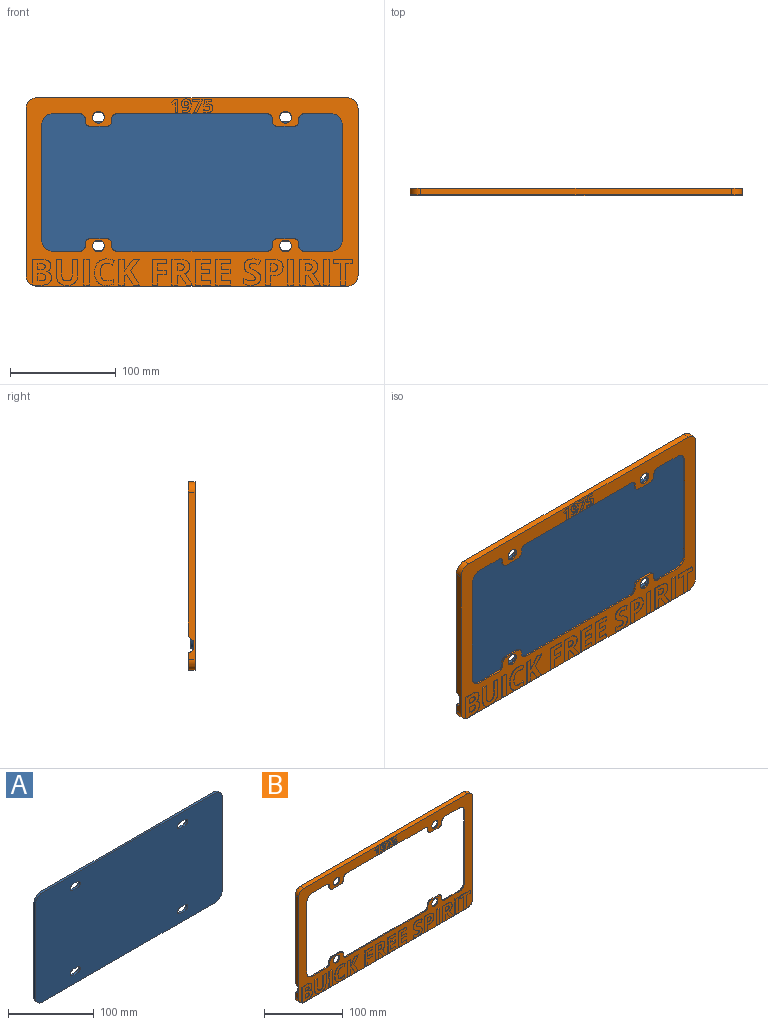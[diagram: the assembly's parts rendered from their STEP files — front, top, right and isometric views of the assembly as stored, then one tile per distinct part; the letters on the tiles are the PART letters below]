
ASSEMBLY  parts=2 mates=1
PART A: 26 faces, bbox 308x3x156 mm
  f0: plane 284x3mm, normal (0,0,1), area 852mm2, adj f1,f23,f24,f25
  f1: cylinder r=12mm len=12mm, axis (0,1,0), area 56.5mm2, adj f0,f2,f24,f25
  f2: plane 132x3mm, normal (-1,0,0), area 396mm2, adj f1,f3,f24,f25
  f3: cylinder r=12mm len=12mm, axis (0,1,0), area 56.5mm2, adj f2,f4,f24,f25
  f4: plane 284x3mm, normal (0,0,-1), area 852mm2, adj f3,f5,f24,f25
  f5: cylinder r=12mm len=12mm, axis (0,1,0), area 56.5mm2, adj f4,f6,f24,f25
  f6: plane 132x3mm, normal (1,0,0), area 396mm2, adj f5,f23,f24,f25
  f7: plane 8x3mm, normal (0,0,-1), area 24mm2, adj f8,f19,f24,f25
  f8: cylinder r=4.25mm len=8.5mm, axis (0,1,0), area 40.1mm2, adj f7,f9,f24,f25
  f9: plane 8x3mm, normal (0,0,1), area 24mm2, adj f8,f19,f24,f25
  f10: cylinder r=4.25mm len=8.5mm, axis (0,1,0), area 40.1mm2, adj f11,f20,f24,f25
  f11: plane 8x3mm, normal (0,0,1), area 24mm2, adj f10,f12,f24,f25
  f12: cylinder r=4.25mm len=8.5mm, axis (0,1,0), area 40.1mm2, adj f11,f20,f24,f25
  f13: plane 8x3mm, normal (0,0,-1), area 24mm2, adj f14,f21,f24,f25
  f14: cylinder r=4.25mm len=8.5mm, axis (0,1,0), area 40.1mm2, adj f13,f15,f24,f25
  f15: plane 8x3mm, normal (0,0,1), area 24mm2, adj f14,f21,f24,f25
  f16: cylinder r=4.25mm len=8.5mm, axis (0,1,0), area 40.1mm2, adj f17,f22,f24,f25
  f17: plane 8x3mm, normal (0,0,-1), area 24mm2, adj f16,f18,f24,f25
  f18: cylinder r=4.25mm len=8.5mm, axis (0,1,0), area 40.1mm2, adj f17,f22,f24,f25
  f19: cylinder r=4.25mm len=8.5mm, axis (0,1,0), area 40.1mm2, adj f7,f9,f24,f25
  f20: plane 8x3mm, normal (0,0,-1), area 24mm2, adj f10,f12,f24,f25
  f21: cylinder r=4.25mm len=8.5mm, axis (0,1,0), area 40.1mm2, adj f13,f15,f24,f25
  f22: plane 8x3mm, normal (0,0,1), area 24mm2, adj f16,f18,f24,f25
  f23: cylinder r=12mm len=12mm, axis (0,1,0), area 56.5mm2, adj f0,f6,f24,f25
  f24: plane 308x156mm, normal (0,-1,0), area 47425.4mm2, adj f0,f1,f2,f3,f4,f5,f6,f7
  f25: plane 308x156mm, normal (0,1,0), area 47425.4mm2, adj f0,f1,f2,f3,f4,f5,f6,f7
PART B: 372 faces, bbox 314x7x178 mm
  f0: plane 314x178mm, normal (0,-1,0), area 16011.1mm2, adj f2,f3,f4,f5,f6,f7,f8,f9
  f1: plane 314x152mm, normal (0,1,0), area 10253mm2, adj f2,f3,f4,f5,f8,f9,f10,f11
  f2: plane 26x1.6mm, normal (0,0,1), area 41.6mm2, adj f0,f1,f16,f32
  f3: plane 142x1.6mm, normal (0,0,1), area 227.2mm2, adj f0,f1,f31,f35
  f4: plane 142x1.6mm, normal (0,0,-1), area 227.2mm2, adj f0,f1,f39,f45
  f5: plane 26x1.6mm, normal (0,0,-1), area 41.6mm2, adj f0,f1,f12,f43
  f6: plane 294x6.4mm, normal (0,0,1), area 1881.6mm2, adj f0,f7,f18,f126
  f7: cylinder r=10mm len=10mm, axis (0,1,0), area 100.5mm2, adj f0,f6,f8,f126
  f8: plane 158x6.4mm, normal (-1,0,0), area 953mm2, adj f0,f1,f7,f120,f126,f128,f137,f369
  f9: plane 158x6.4mm, normal (1,0,0), area 953mm2, adj f0,f1,f18,f121,f126,f127,f139,f369
  f10: cylinder r=10mm len=10mm, axis (0,1,0), area 25.1mm2, adj f0,f1,f11,f17
  f11: plane 110x1.6mm, normal (1,0,0), area 176mm2, adj f0,f1,f10,f12
  f12: cylinder r=10mm len=10mm, axis (0,1,0), area 25.1mm2, adj f0,f1,f5,f11
  f13: plane 26x1.6mm, normal (0,0,-1), area 41.6mm2, adj f0,f1,f14,f41
  f14: cylinder r=10mm len=10mm, axis (0,1,0), area 25.1mm2, adj f0,f1,f13,f15
  f15: plane 110x1.6mm, normal (-1,0,0), area 176mm2, adj f0,f1,f14,f16
  f16: cylinder r=10mm len=10mm, axis (0,1,0), area 25.1mm2, adj f0,f1,f2,f15
  f17: plane 26x1.6mm, normal (0,0,1), area 41.6mm2, adj f0,f1,f10,f37
  f18: cylinder r=10mm len=10mm, axis (0,1,0), area 100.5mm2, adj f0,f6,f9,f126
  f19: plane 2x1.6mm, normal (-1,0,0), area 3.2mm2, adj f0,f1,f43,f44
  f20: plane 15x1.6mm, normal (0,0,-1), area 24mm2, adj f0,f1,f44,f46
  f21: plane 2x1.6mm, normal (1,0,0), area 3.2mm2, adj f0,f1,f45,f46
  f22: plane 2x1.6mm, normal (-1,0,0), area 3.2mm2, adj f0,f1,f39,f40
  f23: plane 15x1.6mm, normal (0,0,-1), area 24mm2, adj f0,f1,f40,f42
  f24: plane 2x1.6mm, normal (1,0,0), area 3.2mm2, adj f0,f1,f41,f42
  f25: plane 2x1.6mm, normal (1,0,0), area 3.2mm2, adj f0,f1,f35,f36
  f26: plane 15x1.6mm, normal (0,0,1), area 24mm2, adj f0,f1,f36,f38
  f27: plane 2x1.6mm, normal (-1,0,0), area 3.2mm2, adj f0,f1,f37,f38
  f28: plane 2x1.6mm, normal (-1,0,0), area 3.2mm2, adj f0,f1,f31,f33
  f29: plane 2x1.6mm, normal (1,0,0), area 3.2mm2, adj f0,f1,f32,f34
  f30: plane 15x1.6mm, normal (0,0,1), area 24mm2, adj f0,f1,f33,f34
  f31: cylinder r=5mm len=5mm, axis (0,-1,0), area 12.6mm2, adj f0,f1,f3,f28
  f32: cylinder r=5mm len=5mm, axis (0,1,0), area 12.6mm2, adj f0,f1,f2,f29
  f33: cylinder r=5mm len=5mm, axis (0,-1,0), area 12.6mm2, adj f0,f1,f28,f30
  f34: cylinder r=5mm len=5mm, axis (0,1,0), area 12.6mm2, adj f0,f1,f29,f30
  f35: cylinder r=5mm len=5mm, axis (0,1,0), area 12.6mm2, adj f0,f1,f3,f25
  f36: cylinder r=5mm len=5mm, axis (0,1,0), area 12.6mm2, adj f0,f1,f25,f26
  f37: cylinder r=5mm len=5mm, axis (0,-1,0), area 12.6mm2, adj f0,f1,f17,f27
  f38: cylinder r=5mm len=5mm, axis (0,-1,0), area 12.6mm2, adj f0,f1,f26,f27
  f39: cylinder r=5mm len=5mm, axis (0,1,0), area 12.6mm2, adj f0,f1,f4,f22
  f40: cylinder r=5mm len=5mm, axis (0,-1,0), area 12.6mm2, adj f0,f1,f22,f23
  f41: cylinder r=5mm len=5mm, axis (0,-1,0), area 12.6mm2, adj f0,f1,f13,f24
  f42: cylinder r=5mm len=5mm, axis (0,1,0), area 12.6mm2, adj f0,f1,f23,f24
  f43: cylinder r=5mm len=5mm, axis (0,1,0), area 12.6mm2, adj f0,f1,f5,f19
  f44: cylinder r=5mm len=5mm, axis (0,-1,0), area 12.6mm2, adj f0,f1,f19,f20
  f45: cylinder r=5mm len=5mm, axis (0,-1,0), area 12.6mm2, adj f0,f1,f4,f21
  f46: cylinder r=5mm len=5mm, axis (0,1,0), area 12.6mm2, adj f0,f1,f20,f21
  f47: cylinder r=5.5mm len=11mm, axis (0,-1,0), area 55.3mm2, adj f0,f1
  f48: cylinder r=5.5mm len=11mm, axis (0,-1,0), area 55.3mm2, adj f0,f1
  f49: cylinder r=5.5mm len=11mm, axis (0,-1,0), area 55.3mm2, adj f0,f1
  f50: cylinder r=5.5mm len=11mm, axis (0,-1,0), area 55.3mm2, adj f0,f1
  f51: plane 2.73x0.6mm, normal (0,0,-1), area 1.6mm2, adj f0,f52,f60,f61
  f52: plane 12.89x0.6mm, normal (1,0,0), area 7.7mm2, adj f0,f51,f53,f61
  f53: plane 2.24x0.6mm, normal (0,0,1), area 1.3mm2, adj f0,f52,f54,f61
  f54: plane 4.15x3.31mm, normal (-0.62,0,0.78), area 3.2mm2, adj f0,f53,f55,f61
  f55: plane 1.64x1.31mm, normal (-0.78,0,-0.63), area 1.3mm2, adj f0,f54,f56,f61
  f56: plane 1.48x1.19mm, normal (0.63,0,-0.78), area 1.1mm2, adj f0,f55,f57,f61
  f57: extruded ~0.94x0.89mm, area 0.8mm2, adj f0,f56,f58,f61
  f58: plane 1.34x0.6mm, normal (-1,0,0.03), area 0.8mm2, adj f0,f57,f59,f61
  f59: plane 1.22x0.6mm, normal (-1,0,0.02), area 0.7mm2, adj f0,f58,f60,f61
  f60: plane 7.46x0.6mm, normal (-1,0,0), area 4.5mm2, adj f0,f51,f59,f61
  f61: plane 12.89x6.39mm, normal (0,-1,0), area 43mm2, adj f51,f52,f53,f54,f55,f56,f57,f58
  f62: extruded ~1.32x0.6mm, area 0.9mm2, adj f63,f87,f88,f89
  f63: extruded ~1.41x0.72mm, area 1mm2, adj f62,f64,f88,f89
  f64: extruded ~1.77x0.6mm, area 1.1mm2, adj f63,f65,f88,f89
  f65: extruded ~1.25x0.6mm, area 0.9mm2, adj f64,f66,f88,f89
  f66: extruded ~1.42x0.6mm, area 0.9mm2, adj f65,f67,f88,f89
  f67: extruded ~1.31x0.6mm, area 0.9mm2, adj f66,f68,f88,f89
  f68: extruded ~1.48x0.6mm, area 0.9mm2, adj f67,f87,f88,f89
  f69: extruded ~5.69x1.6mm, area 3.6mm2, adj f0,f70,f86,f88
  f70: extruded ~3.04x0.6mm, area 1.9mm2, adj f0,f69,f71,f88
  f71: extruded ~1.94x1.64mm, area 1.6mm2, adj f0,f70,f72,f88
  f72: extruded ~2.5x0.67mm, area 1.6mm2, adj f0,f71,f73,f88
  f73: extruded ~3.2x1.2mm, area 2.1mm2, adj f0,f72,f74,f88
  f74: extruded ~3.28x1.18mm, area 2.1mm2, adj f0,f73,f75,f88
  f75: extruded ~3x0.97mm, area 1.9mm2, adj f0,f74,f76,f88
  f76: extruded ~2.65x1.08mm, area 1.8mm2, adj f0,f75,f77,f88
  f77: extruded ~1.67x0.6mm, area 1mm2, adj f0,f76,f78,f88
  f78: extruded ~1.18x1.16mm, area 1mm2, adj f0,f77,f79,f88
  f79: plane 0.6x0.11mm, normal (0,0,-1), area 0.1mm2, adj f0,f78,f80,f88
  f80: extruded ~2.37x0.6mm, area 1.5mm2, adj f0,f79,f81,f88
  f81: extruded ~1.35x1.26mm, area 1.1mm2, adj f0,f80,f82,f88
  f82: extruded ~2.25x0.6mm, area 1.4mm2, adj f0,f81,f83,f88
  f83: extruded ~1.55x0.6mm, area 0.9mm2, adj f0,f82,f84,f88
  f84: plane 2.19x0.6mm, normal (-1,0,0), area 1.3mm2, adj f0,f83,f85,f88
  f85: extruded ~1.74x0.6mm, area 1mm2, adj f0,f84,f86,f88
  f86: extruded ~4.86x1.88mm, area 3.2mm2, adj f0,f69,f85,f88
  f87: extruded ~1.67x0.6mm, area 1.1mm2, adj f62,f68,f88,f89
  f88: plane 13.22x9.1mm, normal (0,-1,0), area 70.9mm2, adj f62,f63,f64,f65,f66,f67,f68,f69
  f89: plane 4.29x3.76mm, normal (0,-1,0), area 13mm2, adj f62,f63,f64,f65,f66,f67,f68,f87
  f90: plane 10.58x4.84mm, normal (-0.91,0,0.42), area 7mm2, adj f0,f91,f96,f97
  f91: plane 2.86x0.6mm, normal (0,0,-1), area 1.7mm2, adj f0,f90,f92,f97
  f92: plane 11.16x4.88mm, normal (0.92,0,-0.4), area 7.3mm2, adj f0,f91,f93,f97
  f93: plane 1.71x0.6mm, normal (1,0,0), area 1mm2, adj f0,f92,f94,f97
  f94: plane 9.25x0.6mm, normal (0,0,1), area 5.5mm2, adj f0,f93,f95,f97
  f95: plane 2.29x0.6mm, normal (-1,0,0), area 1.4mm2, adj f0,f94,f96,f97
  f96: plane 6.36x0.6mm, normal (0,0,-1), area 3.8mm2, adj f0,f90,f95,f97
  f97: plane 12.87x9.25mm, normal (0,-1,0), area 50.2mm2, adj f90,f91,f92,f93,f94,f95,f96
  f98: extruded ~2.98x1.05mm, area 1.9mm2, adj f0,f99,f117,f118
  f99: extruded ~1.33x0.6mm, area 0.8mm2, adj f0,f98,f100,f118
  f100: plane 0.6x0.31mm, normal (-0.2,0,0.98), area 0.2mm2, adj f0,f99,f101,f118
  f101: plane 2.53x0.6mm, normal (1,0,-0.09), area 1.5mm2, adj f0,f100,f102,f118
  f102: plane 4.6x0.6mm, normal (0,0,-1), area 2.8mm2, adj f0,f101,f103,f118
  f103: plane 2.31x0.6mm, normal (1,0,0), area 1.4mm2, adj f0,f102,f104,f118
  f104: plane 6.99x0.6mm, normal (0,0,1), area 4.2mm2, adj f0,f103,f105,f118
  f105: plane 6.57x0.6mm, normal (-1,0,0.07), area 4mm2, adj f0,f104,f106,f118
  f106: plane 1.09x0.6mm, normal (-0.47,0,-0.88), area 0.7mm2, adj f0,f105,f107,f118
  f107: extruded ~0.92x0.6mm, area 0.6mm2, adj f0,f106,f108,f118
  f108: extruded ~1.03x0.6mm, area 0.6mm2, adj f0,f107,f109,f118
  f109: extruded ~2.58x1.95mm, area 2.2mm2, adj f0,f108,f110,f118
  f110: extruded ~2.5x2.05mm, area 2.2mm2, adj f0,f109,f111,f118
  f111: extruded ~1.75x0.6mm, area 1.1mm2, adj f0,f110,f112,f118
  f112: extruded ~1.62x0.6mm, area 1mm2, adj f0,f111,f113,f118
  f113: plane 2.36x0.6mm, normal (-1,0,0), area 1.4mm2, adj f0,f112,f114,f118
  f114: extruded ~3.47x0.7mm, area 2.1mm2, adj f0,f113,f115,f118
  f115: extruded ~3.81x1.17mm, area 2.4mm2, adj f0,f114,f116,f118
  f116: extruded ~3.32x1.33mm, area 2.2mm2, adj f0,f115,f117,f118
  f117: extruded ~2.87x1.11mm, area 1.9mm2, adj f0,f98,f116,f118
  f118: plane 13.07x8.61mm, normal (0,-1,0), area 65.6mm2, adj f98,f99,f100,f101,f102,f103,f104,f105
  f119: plane 137.6x1.8mm, normal (1,0,0), area 171.1mm2, adj f125,f126,f128,f133,f135,f136,f368
  f120: plane 5x0.6mm, normal (0,0,-1), area 2.3mm2, adj f1,f8,f128,f368
  f121: plane 5x0.6mm, normal (0,0,-1), area 2.3mm2, adj f1,f9,f127,f364
  f122: plane 137.6x1.8mm, normal (-1,0,0), area 171.1mm2, adj f123,f126,f127,f129,f131,f132,f364
  f123: cylinder r=8mm len=8mm, axis (0,-1,0), area 22.6mm2, adj f122,f124,f126,f365
  f124: plane 294x1.8mm, normal (0,0,-1), area 529.2mm2, adj f123,f125,f126,f366
  f125: cylinder r=8mm len=8mm, axis (0,-1,0), area 22.6mm2, adj f119,f124,f126,f367
  f126: plane 314x145.8mm, normal (0,1,0), area 1787.7mm2, adj f6,f7,f8,f9,f18,f119,f122,f123
  f127: plane 4.2x4.2mm, normal (0,0.71,-0.71), area 13.1mm2, adj f9,f121,f122,f126,f364
  f128: plane 4.2x4.2mm, normal (0,0.71,-0.71), area 13.1mm2, adj f8,f119,f120,f126,f368
  f129: plane 75x4mm, normal (0,-1,0), area 300mm2, adj f122,f130,f131,f132
  f130: plane 75x1mm, normal (-1,0,0), area 75mm2, adj f126,f129,f131,f132
  f131: plane 4x1mm, normal (0,0,1), area 4mm2, adj f122,f126,f129,f130
  f132: plane 4x1mm, normal (0,0,-1), area 4mm2, adj f122,f126,f129,f130
  f133: plane 75x4mm, normal (0,-1,0), area 300mm2, adj f119,f134,f135,f136
  f134: plane 75x1mm, normal (1,0,0), area 75mm2, adj f126,f133,f135,f136
  f135: plane 4x1mm, normal (0,0,1), area 4mm2, adj f119,f126,f133,f134
  f136: plane 4x1mm, normal (0,0,-1), area 4mm2, adj f119,f126,f133,f134
  f137: cylinder r=10mm len=10mm, axis (0,-1,0), area 100.5mm2, adj f0,f8,f138,f369
  f138: plane 294x6.4mm, normal (0,0,-1), area 1881.6mm2, adj f0,f137,f139,f369
  f139: cylinder r=10mm len=10mm, axis (0,-1,0), area 100.5mm2, adj f0,f9,f138,f369
  f140: plane 6.34x0.6mm, normal (1,0,0), area 3.8mm2, adj f141,f164,f165,f166
  f141: plane 3.2x0.6mm, normal (0,0,-1), area 1.9mm2, adj f140,f142,f165,f166
  f142: extruded ~4.33x3.03mm, area 3.6mm2, adj f141,f143,f165,f166
  f143: extruded ~2.5x1.02mm, area 1.7mm2, adj f142,f144,f165,f166
  f144: extruded ~3.15x0.82mm, area 2mm2, adj f143,f164,f165,f166
  f145: plane 2.99x0.6mm, normal (0,0,1), area 1.8mm2, adj f146,f162,f165,f167
  f146: plane 5.41x0.6mm, normal (1,0,0), area 3.2mm2, adj f145,f147,f165,f167
  f147: plane 2.71x0.6mm, normal (0,0,-1), area 1.6mm2, adj f146,f148,f165,f167
  f148: extruded ~3.24x0.61mm, area 2mm2, adj f147,f149,f165,f167
  f149: extruded ~2.01x1.02mm, area 1.4mm2, adj f148,f150,f165,f167
  f150: extruded ~2.15x0.94mm, area 1.5mm2, adj f149,f162,f165,f167
  f151: plane 7.58x0.6mm, normal (0,0,1), area 4.5mm2, adj f0,f152,f163,f165
  f152: plane 24.34x0.6mm, normal (-1,0,0), area 14.6mm2, adj f0,f151,f153,f165
  f153: plane 9.1x0.6mm, normal (0,0,-1), area 5.5mm2, adj f0,f152,f154,f165
  f154: extruded ~6.54x1.86mm, area 4.2mm2, adj f0,f153,f155,f165
  f155: extruded ~5.19x2.41mm, area 3.6mm2, adj f0,f154,f156,f165
  f156: extruded ~3.76x1.03mm, area 2.4mm2, adj f0,f155,f157,f165
  f157: extruded ~3.34x1.93mm, area 2.4mm2, adj f0,f156,f158,f165
  f158: plane 0.6x0.17mm, normal (1,0,0), area 0.1mm2, adj f0,f157,f159,f165
  f159: extruded ~2.72x1.68mm, area 2mm2, adj f0,f158,f160,f165
  f160: extruded ~3.58x1.02mm, area 2.3mm2, adj f0,f159,f161,f165
  f161: extruded ~4.69x2.34mm, area 3.3mm2, adj f0,f160,f163,f165
  f162: extruded ~3.04x0.65mm, area 1.9mm2, adj f145,f150,f165,f167
  f163: extruded ~7.52x1.47mm, area 4.7mm2, adj f0,f151,f161,f165
  f164: plane 3.36x0.6mm, normal (0,0,1), area 2mm2, adj f140,f144,f165,f166
  f165: plane 24.34x18.05mm, normal (0,-1,0), area 323mm2, adj f140,f141,f142,f143,f144,f145,f146,f147
  f166: plane 7.52x6.34mm, normal (0,-1,0), area 43.3mm2, adj f140,f141,f142,f143,f144,f164
  f167: plane 6.97x5.41mm, normal (0,-1,0), area 34.4mm2, adj f145,f146,f147,f148,f149,f150,f162
  f168: plane 15.75x0.6mm, normal (1,0,0), area 9.4mm2, adj f0,f169,f182,f183
  f169: plane 5.15x0.6mm, normal (0,0,1), area 3.1mm2, adj f0,f168,f170,f183
  f170: plane 14.87x0.6mm, normal (-1,0,0), area 8.9mm2, adj f0,f169,f171,f183
  f171: extruded ~4.15x1.14mm, area 2.6mm2, adj f0,f170,f172,f183
  f172: extruded ~3.67x1.32mm, area 2.4mm2, adj f0,f171,f173,f183
  f173: extruded ~3.75x1.32mm, area 2.5mm2, adj f0,f172,f174,f183
  f174: extruded ~4.13x1.13mm, area 2.6mm2, adj f0,f173,f175,f183
  f175: plane 14.9x0.6mm, normal (1,0,0), area 8.9mm2, adj f0,f174,f176,f183
  f176: plane 5.14x0.6mm, normal (0,0,1), area 3.1mm2, adj f0,f175,f177,f183
  f177: plane 15.68x0.6mm, normal (-1,0,0), area 9.4mm2, adj f0,f176,f178,f183
  f178: extruded ~6.58x2.6mm, area 4.4mm2, adj f0,f177,f179,f183
  f179: extruded ~7.29x2.41mm, area 4.7mm2, adj f0,f178,f180,f183
  f180: extruded ~5.39x1.08mm, area 3.3mm2, adj f0,f179,f181,f183
  f181: extruded ~3.49x3.11mm, area 2.8mm2, adj f0,f180,f182,f183
  f182: extruded ~4.73x1.21mm, area 3mm2, adj f0,f168,f181,f183
  f183: plane 24.68x19.98mm, normal (0,-1,0), area 271.1mm2, adj f168,f169,f170,f171,f172,f173,f174,f175
  f184: plane 24.34x0.6mm, normal (-1,0,0), area 14.6mm2, adj f0,f185,f187,f188
  f185: plane 5.16x0.6mm, normal (0,0,-1), area 3.1mm2, adj f0,f184,f186,f188
  f186: plane 24.34x0.6mm, normal (1,0,0), area 14.6mm2, adj f0,f185,f187,f188
  f187: plane 5.16x0.6mm, normal (0,0,1), area 3.1mm2, adj f0,f184,f186,f188
  f188: plane 24.34x5.16mm, normal (0,-1,0), area 125.6mm2, adj f184,f185,f186,f187
  f189: extruded ~4.51x2.19mm, area 3.1mm2, adj f0,f190,f203,f204
  f190: extruded ~2.71x0.6mm, area 1.7mm2, adj f0,f189,f191,f204
  f191: extruded ~2.75x1.13mm, area 1.8mm2, adj f0,f190,f192,f204
  f192: plane 4.2x1.66mm, normal (0.93,0,-0.37), area 2.7mm2, adj f0,f191,f193,f204
  f193: extruded ~7.12x1.71mm, area 4.4mm2, adj f0,f192,f194,f204
  f194: extruded ~6.07x1.52mm, area 3.8mm2, adj f0,f193,f195,f204
  f195: extruded ~4.38x3.97mm, area 3.6mm2, adj f0,f194,f196,f204
  f196: extruded ~6.65x1.38mm, area 4.1mm2, adj f0,f195,f197,f204
  f197: extruded ~9.25x2.81mm, area 5.9mm2, adj f0,f196,f198,f204
  f198: extruded ~8.12x3.22mm, area 5.4mm2, adj f0,f197,f199,f204
  f199: extruded ~6.69x1.25mm, area 4.1mm2, adj f0,f198,f200,f204
  f200: plane 4.33x0.6mm, normal (1,0,0), area 2.6mm2, adj f0,f199,f201,f204
  f201: extruded ~6.21x1.28mm, area 3.8mm2, adj f0,f200,f202,f204
  f202: extruded ~8.14x6.11mm, area 7mm2, adj f0,f201,f203,f204
  f203: extruded ~6.1x1.6mm, area 3.8mm2, adj f0,f189,f202,f204
  f204: plane 25.02x18.54mm, normal (0,-1,0), area 208mm2, adj f189,f190,f191,f192,f193,f194,f195,f196
  f205: plane 5.86x0.6mm, normal (0,0,-1), area 3.5mm2, adj f0,f206,f217,f218
  f206: plane 13.57x8.56mm, normal (0.85,0,0.53), area 9.6mm2, adj f0,f205,f207,f218
  f207: plane 10.77x8.49mm, normal (0.79,0,-0.62), area 8.2mm2, adj f0,f206,f208,f218
  f208: plane 5.73x0.6mm, normal (0,0,1), area 3.4mm2, adj f0,f207,f209,f218
  f209: plane 8.27x6.6mm, normal (-0.78,0,0.62), area 6.3mm2, adj f0,f208,f210,f218
  f210: plane 2.87x2.03mm, normal (-0.82,0,0.58), area 2.1mm2, adj f0,f209,f211,f218
  f211: plane 11.14x0.6mm, normal (1,0,0), area 6.7mm2, adj f0,f210,f212,f218
  f212: plane 5.16x0.6mm, normal (0,0,1), area 3.1mm2, adj f0,f211,f213,f218
  f213: plane 24.34x0.6mm, normal (-1,0,0), area 14.6mm2, adj f0,f212,f214,f218
  f214: plane 5.16x0.6mm, normal (0,0,-1), area 3.1mm2, adj f0,f213,f215,f218
  f215: plane 8.69x0.6mm, normal (1,0,0), area 5.2mm2, adj f0,f214,f216,f218
  f216: plane 2.18x1.57mm, normal (0.58,0,-0.81), area 1.6mm2, adj f0,f215,f217,f218
  f217: plane 10.25x6.38mm, normal (-0.85,0,-0.53), area 7.2mm2, adj f0,f205,f216,f218
  f218: plane 24.34x19.58mm, normal (0,-1,0), area 271.7mm2, adj f205,f206,f207,f208,f209,f210,f211,f212
  f219: plane 5.08x0.6mm, normal (0,0,-1), area 3mm2, adj f0,f220,f228,f229
  f220: plane 9.62x0.6mm, normal (1,0,0), area 5.8mm2, adj f0,f219,f221,f229
  f221: plane 8.26x0.6mm, normal (0,0,-1), area 5mm2, adj f0,f220,f222,f229
  f222: plane 4.21x0.6mm, normal (1,0,0), area 2.5mm2, adj f0,f221,f223,f229
  f223: plane 8.26x0.6mm, normal (0,0,1), area 5mm2, adj f0,f222,f224,f229
  f224: plane 6.28x0.6mm, normal (1,0,0), area 3.8mm2, adj f0,f223,f225,f229
  f225: plane 8.88x0.6mm, normal (0,0,-1), area 5.3mm2, adj f0,f224,f226,f229
  f226: plane 4.23x0.6mm, normal (1,0,0), area 2.5mm2, adj f0,f225,f227,f229
  f227: plane 13.95x0.6mm, normal (0,0,1), area 8.4mm2, adj f0,f226,f228,f229
  f228: plane 24.34x0.6mm, normal (-1,0,0), area 14.6mm2, adj f0,f219,f227,f229
  f229: plane 24.34x13.95mm, normal (0,-1,0), area 195.9mm2, adj f219,f220,f221,f222,f223,f224,f225,f226
  f230: plane 9.34x0.6mm, normal (1,0,0), area 5.6mm2, adj f0,f231,f248,f249
  f231: plane 2.74x0.6mm, normal (0,0,-1), area 1.6mm2, adj f0,f230,f232,f249
  f232: plane 9.34x5.81mm, normal (-0.85,0,-0.53), area 6.6mm2, adj f0,f231,f233,f249
  f233: plane 5.73x0.6mm, normal (0,0,-1), area 3.4mm2, adj f0,f232,f234,f249
  f234: extruded ~10.61x7.16mm, area 7.7mm2, adj f0,f233,f235,f249
  f235: extruded ~3.35x2.62mm, area 2.6mm2, adj f0,f234,f236,f249
  f236: extruded ~3.82x1.18mm, area 2.4mm2, adj f0,f235,f237,f249
  f237: extruded ~5.49x2.38mm, area 3.7mm2, adj f0,f236,f238,f249
  f238: extruded ~7.34x1.81mm, area 4.6mm2, adj f0,f237,f239,f249
  f239: plane 7.09x0.6mm, normal (0,0,1), area 4.3mm2, adj f0,f238,f240,f249
  f240: plane 24.34x0.6mm, normal (-1,0,0), area 14.6mm2, adj f0,f239,f248,f249
  f241: plane 1.66x0.6mm, normal (0,0,1), area 1mm2, adj f242,f247,f249,f250
  f242: plane 6.57x0.6mm, normal (1,0,0), area 3.9mm2, adj f241,f243,f249,f250
  f243: plane 1.57x0.6mm, normal (0,0,-1), area 0.9mm2, adj f242,f244,f249,f250
  f244: extruded ~3.68x0.73mm, area 2.3mm2, adj f243,f245,f249,f250
  f245: extruded ~2.46x1.19mm, area 1.7mm2, adj f244,f246,f249,f250
  f246: extruded ~2.56x1.16mm, area 1.8mm2, adj f245,f247,f249,f250
  f247: extruded ~3.61x0.82mm, area 2.3mm2, adj f241,f246,f249,f250
  f248: plane 5.16x0.6mm, normal (0,0,-1), area 3.1mm2, adj f0,f230,f240,f249
  f249: plane 24.34x19.44mm, normal (0,-1,0), area 289.3mm2, adj f230,f231,f232,f233,f234,f235,f236,f237
  f250: plane 6.57x6.44mm, normal (0,-1,0), area 37.4mm2, adj f241,f242,f243,f244,f245,f246,f247
  f251: plane 14.02x0.6mm, normal (0,0,-1), area 8.4mm2, adj f0,f252,f262,f263
  f252: plane 4.26x0.6mm, normal (1,0,0), area 2.6mm2, adj f0,f251,f253,f263
  f253: plane 8.85x0.6mm, normal (0,0,1), area 5.3mm2, adj f0,f252,f254,f263
  f254: plane 6.28x0.6mm, normal (1,0,0), area 3.8mm2, adj f0,f253,f255,f263
  f255: plane 8.24x0.6mm, normal (0,0,-1), area 4.9mm2, adj f0,f254,f256,f263
  f256: plane 4.23x0.6mm, normal (1,0,0), area 2.5mm2, adj f0,f255,f257,f263
  f257: plane 8.24x0.6mm, normal (0,0,1), area 4.9mm2, adj f0,f256,f258,f263
  f258: plane 5.34x0.6mm, normal (1,0,0), area 3.2mm2, adj f0,f257,f259,f263
  f259: plane 8.85x0.6mm, normal (0,0,-1), area 5.3mm2, adj f0,f258,f260,f263
  f260: plane 4.23x0.6mm, normal (1,0,0), area 2.5mm2, adj f0,f259,f261,f263
  f261: plane 14.02x0.6mm, normal (0,0,1), area 8.4mm2, adj f0,f260,f262,f263
  f262: plane 24.34x0.6mm, normal (-1,0,0), area 14.6mm2, adj f0,f251,f261,f263
  f263: plane 24.34x14.02mm, normal (0,-1,0), area 235.7mm2, adj f251,f252,f253,f254,f255,f256,f257,f258
  f264: plane 14.02x0.6mm, normal (0,0,-1), area 8.4mm2, adj f0,f265,f275,f276
  f265: plane 4.26x0.6mm, normal (1,0,0), area 2.6mm2, adj f0,f264,f266,f276
  f266: plane 8.85x0.6mm, normal (0,0,1), area 5.3mm2, adj f0,f265,f267,f276
  f267: plane 6.28x0.6mm, normal (1,0,0), area 3.8mm2, adj f0,f266,f268,f276
  f268: plane 8.24x0.6mm, normal (0,0,-1), area 4.9mm2, adj f0,f267,f269,f276
  f269: plane 4.23x0.6mm, normal (1,0,0), area 2.5mm2, adj f0,f268,f270,f276
  f270: plane 8.24x0.6mm, normal (0,0,1), area 4.9mm2, adj f0,f269,f271,f276
  f271: plane 5.34x0.6mm, normal (1,0,0), area 3.2mm2, adj f0,f270,f272,f276
  f272: plane 8.85x0.6mm, normal (0,0,-1), area 5.3mm2, adj f0,f271,f273,f276
  f273: plane 4.23x0.6mm, normal (1,0,0), area 2.5mm2, adj f0,f272,f274,f276
  f274: plane 14.02x0.6mm, normal (0,0,1), area 8.4mm2, adj f0,f273,f275,f276
  f275: plane 24.34x0.6mm, normal (-1,0,0), area 14.6mm2, adj f0,f264,f274,f276
  f276: plane 24.34x14.02mm, normal (0,-1,0), area 235.7mm2, adj f264,f265,f266,f267,f268,f269,f270,f271
  f277: extruded ~5.2x2.37mm, area 3.6mm2, adj f0,f278,f304,f305
  f278: extruded ~4.02x1.27mm, area 2.6mm2, adj f0,f277,f279,f305
  f279: extruded ~4.68x3.27mm, area 3.5mm2, adj f0,f278,f280,f305
  f280: extruded ~3.27x1.7mm, area 2.2mm2, adj f0,f279,f281,f305
  f281: extruded ~1.01x0.98mm, area 0.9mm2, adj f0,f280,f282,f305
  f282: extruded ~1.19x0.6mm, area 0.7mm2, adj f0,f281,f283,f305
  f283: extruded ~1.78x0.78mm, area 1.2mm2, adj f0,f282,f284,f305
  f284: extruded ~2.25x0.68mm, area 1.4mm2, adj f0,f283,f285,f305
  f285: extruded ~2.5x0.6mm, area 1.5mm2, adj f0,f284,f286,f305
  f286: extruded ~3.22x1.12mm, area 2mm2, adj f0,f285,f287,f305
  f287: plane 4.02x1.66mm, normal (0.92,0,-0.38), area 2.6mm2, adj f0,f286,f288,f305
  f288: extruded ~3.6x1.26mm, area 2.3mm2, adj f0,f287,f289,f305
  f289: extruded ~3.62x0.6mm, area 2.2mm2, adj f0,f288,f290,f305
  f290: extruded ~6.05x1.85mm, area 3.9mm2, adj f0,f289,f291,f305
  f291: extruded ~5.08x2.19mm, area 3.4mm2, adj f0,f290,f292,f305
  f292: extruded ~2.99x0.67mm, area 1.9mm2, adj f0,f291,f293,f305
  f293: extruded ~2.25x1.78mm, area 1.7mm2, adj f0,f292,f294,f305
  f294: extruded ~3.34x2.01mm, area 2.3mm2, adj f0,f293,f295,f305
  f295: extruded ~3.16x1.65mm, area 2.1mm2, adj f0,f294,f296,f305
  f296: extruded ~1.17x1.07mm, area 1mm2, adj f0,f295,f297,f305
  f297: extruded ~1.27x0.6mm, area 0.8mm2, adj f0,f296,f298,f305
  f298: extruded ~1.93x0.91mm, area 1.3mm2, adj f0,f297,f299,f305
  f299: extruded ~2.6x0.65mm, area 1.6mm2, adj f0,f298,f300,f305
  f300: extruded ~3.12x0.6mm, area 1.9mm2, adj f0,f299,f301,f305
  f301: extruded ~4.17x1.55mm, area 2.7mm2, adj f0,f300,f302,f305
  f302: plane 4.79x0.6mm, normal (-1,0,0), area 2.9mm2, adj f0,f301,f303,f305
  f303: extruded ~6.89x1.47mm, area 4.3mm2, adj f0,f302,f304,f305
  f304: extruded ~6.6x1.9mm, area 4.2mm2, adj f0,f277,f303,f305
  f305: plane 25.02x15.86mm, normal (0,-1,0), area 223.4mm2, adj f277,f278,f279,f280,f281,f282,f283,f284
  f306: extruded ~6.01x2.46mm, area 4mm2, adj f0,f307,f321,f322
  f307: extruded ~5.68x2.3mm, area 3.8mm2, adj f0,f306,f308,f322
  f308: extruded ~6.74x1.91mm, area 4.3mm2, adj f0,f307,f309,f322
  f309: plane 7.77x0.6mm, normal (0,0,1), area 4.7mm2, adj f0,f308,f310,f322
  f310: plane 24.34x0.6mm, normal (-1,0,0), area 14.6mm2, adj f0,f309,f311,f322
  f311: plane 5.16x0.6mm, normal (0,0,-1), area 3.1mm2, adj f0,f310,f312,f322
  f312: plane 8.66x0.6mm, normal (1,0,0), area 5.2mm2, adj f0,f311,f313,f322
  f313: plane 2.21x0.6mm, normal (0,0,-1), area 1.3mm2, adj f0,f312,f321,f322
  f314: plane 1.7x0.6mm, normal (0,0,1), area 1mm2, adj f315,f320,f322,f323
  f315: plane 7.22x0.6mm, normal (1,0,0), area 4.3mm2, adj f314,f316,f322,f323
  f316: plane 2.34x0.6mm, normal (0,0,-1), area 1.4mm2, adj f315,f317,f322,f323
  f317: extruded ~3.11x0.87mm, area 2mm2, adj f316,f318,f322,f323
  f318: extruded ~2.68x0.99mm, area 1.8mm2, adj f317,f319,f322,f323
  f319: extruded ~2.74x1.18mm, area 1.9mm2, adj f318,f320,f322,f323
  f320: extruded ~3.56x0.94mm, area 2.2mm2, adj f314,f319,f322,f323
  f321: extruded ~6.98x2.08mm, area 4.5mm2, adj f0,f306,f313,f322
  f322: plane 24.34x16.81mm, normal (0,-1,0), area 242.1mm2, adj f306,f307,f308,f309,f310,f311,f312,f313
  f323: plane 7.22x6.44mm, normal (0,-1,0), area 41.3mm2, adj f314,f315,f316,f317,f318,f319,f320
  f324: plane 24.34x0.6mm, normal (-1,0,0), area 14.6mm2, adj f0,f325,f327,f328
  f325: plane 5.16x0.6mm, normal (0,0,-1), area 3.1mm2, adj f0,f324,f326,f328
  f326: plane 24.34x0.6mm, normal (1,0,0), area 14.6mm2, adj f0,f325,f327,f328
  f327: plane 5.16x0.6mm, normal (0,0,1), area 3.1mm2, adj f0,f324,f326,f328
  f328: plane 24.34x5.16mm, normal (0,-1,0), area 125.6mm2, adj f324,f325,f326,f327
  f329: plane 9.34x0.6mm, normal (1,0,0), area 5.6mm2, adj f0,f330,f347,f348
  f330: plane 2.74x0.6mm, normal (0,0,-1), area 1.6mm2, adj f0,f329,f331,f348
  f331: plane 9.34x5.81mm, normal (-0.85,0,-0.53), area 6.6mm2, adj f0,f330,f332,f348
  f332: plane 5.73x0.6mm, normal (0,0,-1), area 3.4mm2, adj f0,f331,f333,f348
  f333: extruded ~10.61x7.16mm, area 7.7mm2, adj f0,f332,f334,f348
  f334: extruded ~3.35x2.62mm, area 2.6mm2, adj f0,f333,f335,f348
  f335: extruded ~3.82x1.18mm, area 2.4mm2, adj f0,f334,f336,f348
  f336: extruded ~5.49x2.38mm, area 3.7mm2, adj f0,f335,f337,f348
  f337: extruded ~7.34x1.81mm, area 4.6mm2, adj f0,f336,f338,f348
  f338: plane 7.09x0.6mm, normal (0,0,1), area 4.3mm2, adj f0,f337,f339,f348
  f339: plane 24.34x0.6mm, normal (-1,0,0), area 14.6mm2, adj f0,f338,f347,f348
  f340: plane 1.66x0.6mm, normal (0,0,1), area 1mm2, adj f341,f346,f348,f349
  f341: plane 6.57x0.6mm, normal (1,0,0), area 3.9mm2, adj f340,f342,f348,f349
  f342: plane 1.57x0.6mm, normal (0,0,-1), area 0.9mm2, adj f341,f343,f348,f349
  f343: extruded ~3.68x0.73mm, area 2.3mm2, adj f342,f344,f348,f349
  f344: extruded ~2.46x1.19mm, area 1.7mm2, adj f343,f345,f348,f349
  f345: extruded ~2.56x1.16mm, area 1.8mm2, adj f344,f346,f348,f349
  f346: extruded ~3.61x0.82mm, area 2.3mm2, adj f340,f345,f348,f349
  f347: plane 5.16x0.6mm, normal (0,0,-1), area 3.1mm2, adj f0,f329,f339,f348
  f348: plane 24.34x19.44mm, normal (0,-1,0), area 289.3mm2, adj f329,f330,f331,f332,f333,f334,f335,f336
  f349: plane 6.57x6.44mm, normal (0,-1,0), area 37.4mm2, adj f340,f341,f342,f343,f344,f345,f346
  f350: plane 24.34x0.6mm, normal (-1,0,0), area 14.6mm2, adj f0,f351,f353,f354
  f351: plane 5.16x0.6mm, normal (0,0,-1), area 3.1mm2, adj f0,f350,f352,f354
  f352: plane 24.34x0.6mm, normal (1,0,0), area 14.6mm2, adj f0,f351,f353,f354
  f353: plane 5.16x0.6mm, normal (0,0,1), area 3.1mm2, adj f0,f350,f352,f354
  f354: plane 24.34x5.16mm, normal (0,-1,0), area 125.6mm2, adj f350,f351,f352,f353
  f355: plane 5.16x0.6mm, normal (0,0,-1), area 3.1mm2, adj f0,f356,f362,f363
  f356: plane 20.05x0.6mm, normal (1,0,0), area 12mm2, adj f0,f355,f357,f363
  f357: plane 6.61x0.6mm, normal (0,0,-1), area 4mm2, adj f0,f356,f358,f363
  f358: plane 4.29x0.6mm, normal (1,0,0), area 2.6mm2, adj f0,f357,f359,f363
  f359: plane 18.38x0.6mm, normal (0,0,1), area 11mm2, adj f0,f358,f360,f363
  f360: plane 4.29x0.6mm, normal (-1,0,0), area 2.6mm2, adj f0,f359,f361,f363
  f361: plane 6.61x0.6mm, normal (0,0,-1), area 4mm2, adj f0,f360,f362,f363
  f362: plane 20.05x0.6mm, normal (-1,0,0), area 12mm2, adj f0,f355,f361,f363
  f363: plane 24.34x18.38mm, normal (0,-1,0), area 182.4mm2, adj f355,f356,f357,f358,f359,f360,f361,f362
  f364: cylinder r=3mm len=140mm, axis (0,0,-1), area 656.7mm2, adj f1,f121,f122,f127,f365
  f365: torus R=5mm, axis (0,-1,0), area 51.1mm2, adj f1,f123,f364,f366
  f366: cylinder r=3mm len=294mm, axis (1,0,0), area 1385.4mm2, adj f1,f124,f365,f367
  f367: torus R=5mm, axis (0,-1,0), area 51.1mm2, adj f1,f125,f366,f368
  f368: cylinder r=3mm len=140mm, axis (0,0,1), area 656.7mm2, adj f1,f119,f120,f128,f367
  f369: plane 314x17mm, normal (0,1,0), area 5295.1mm2, adj f8,f9,f137,f138,f139,f370
  f370: plane 314x0.8mm, normal (0,0,1), area 251.2mm2, adj f8,f9,f369,f371
  f371: cylinder r=4mm len=314mm, axis (-1,0,0), area 1972.9mm2, adj f1,f8,f9,f370
PLACE A t=(88.5,4.6,60.75)mm
PLACE B t=(88.5,1.6,60)mm
MATE fastened B.f47 <-> A.f24  axis (0,1,0) through (0,1.6,121.5)mm
